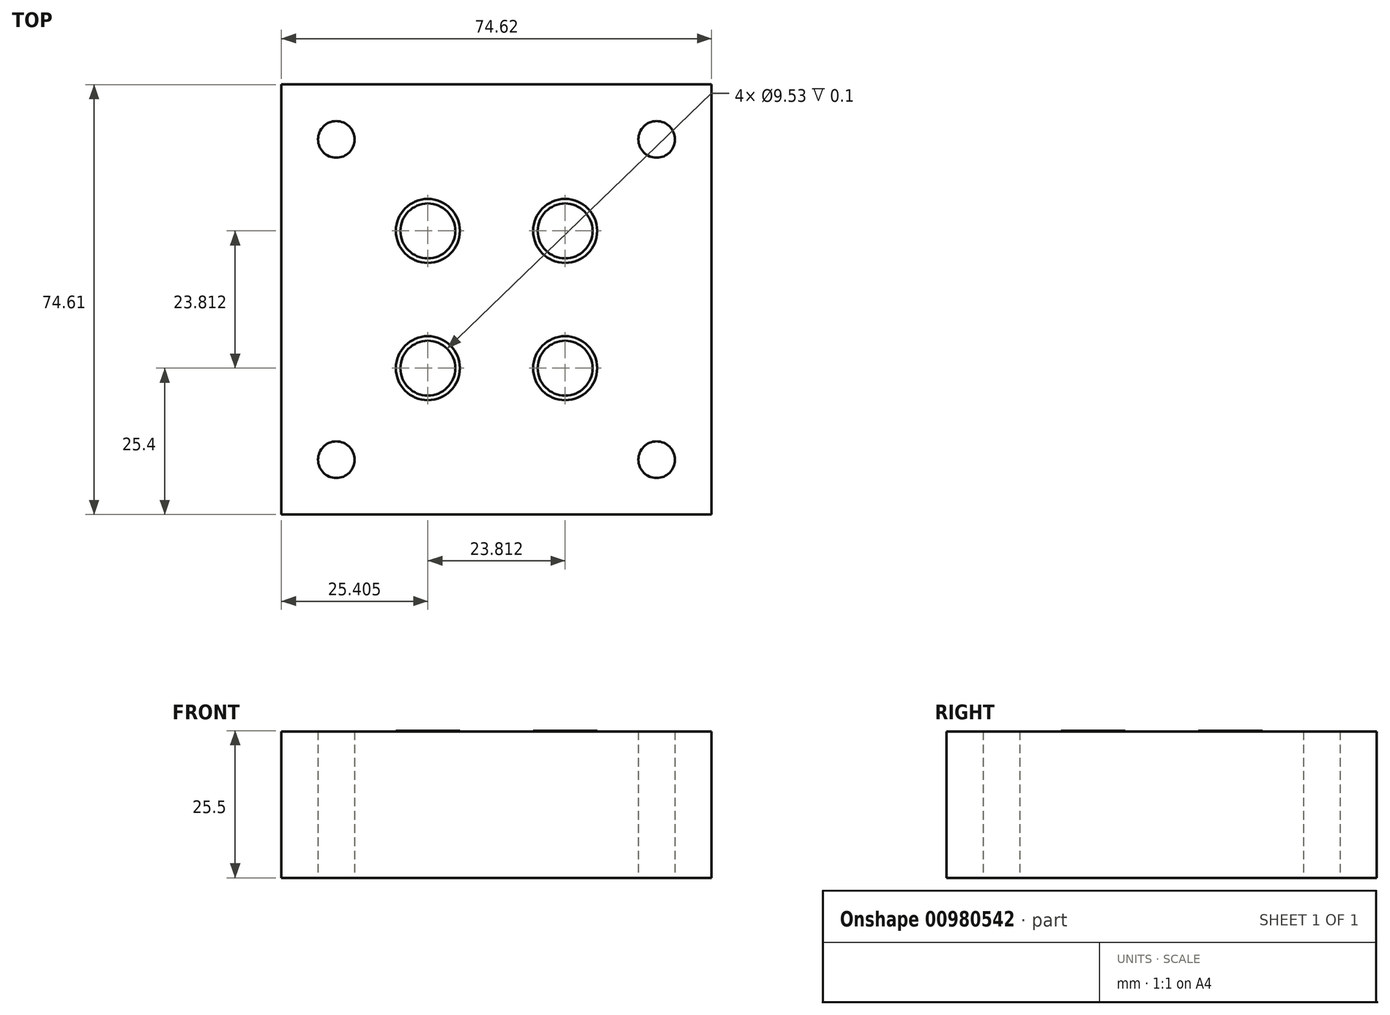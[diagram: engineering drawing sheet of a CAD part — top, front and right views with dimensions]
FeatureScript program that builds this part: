
annotation { "Feature Type Name" : "Feature", "Feature Type Description" : "" }
export const myFeature = defineFeature(function(context is Context, id is Id, definition is map)
    precondition{}
    {
        {
            var Q0;
            Q0=qCreatedBy(makeId("Top.planeOp"),FACE);
            var sketch = newSketch(context, id + "F0", { "sketchPlane" : qUnion([Q0])});
            skLineSegment(sketch, "E0.bottom", {"start": v(-258.87, 74.61) * mm, "end": v(-184.25, 74.61) * mm});
            skLineSegment(sketch, "E0.top", {"start": v(-258.87, 0) * mm, "end": v(-184.25, 0) * mm});
            skLineSegment(sketch, "E0.left", {"start": v(-258.87, 74.61) * mm, "end": v(-258.87, 0) * mm});
            skLineSegment(sketch, "E0.right", {"start": v(-184.25, 74.61) * mm, "end": v(-184.25, 0) * mm});
            skSolve(sketch);
        }
        {
            var Q0;
            Q0=makeQuery(id+"F0.imprint","IMPRINT",FACE,{"disambiguationData":[TD([[makeQuery(id+"F0.imprint","IMPRINT",EDGE,{"derivedFrom":sQuery(id+"F0.wireOp",EDGE,"E0.bottom")}),-1.0]])]});
            extrude(context, id + "F1", {"entities" : qUnion([Q0]), "depth" : 25.4 * mm, "offsetDistance" : 25.4 * mm});
        }
        {
            var Q0;
            Q0=qCreatedBy(makeId("Top.planeOp"),FACE);
            var sketch = newSketch(context, id + "F2", { "sketchPlane" : qUnion([Q0])});
            skCircle(sketch, "E1", {"center": v(-249.34, 65.09) * mm, "radius": 3.18 * mm});
            skCircle(sketch, "E2", {"center": v(-193.78, 65.09) * mm, "radius": 3.18 * mm});
            skCircle(sketch, "E3", {"center": v(-249.34, 9.53) * mm, "radius": 3.18 * mm});
            skCircle(sketch, "E4", {"center": v(-193.78, 9.52) * mm, "radius": 3.18 * mm});
            skSolve(sketch);
        }
        {
            var Q0;
            Q0 = qSketchRegion(id + "F2", true);
            extrude(context, id + "F3", {"entities" : qUnion([Q0]), "operationType" : NewBodyOperationType.REMOVE, "depth" : 25.4 * mm, "offsetDistance" : 25.4 * mm});
        }
        {
            var Q0;
            Q0=makeQuery(id+"F1.opExtrude","CAP_FACE",FACE,{"disambiguationData":[OSD([sQuery(id+"F0.wireOp",EDGE,"E0.bottom"),sQuery(id+"F0.wireOp",EDGE,"E0.top"),sQuery(id+"F0.wireOp",EDGE,"E0.left"),sQuery(id+"F0.wireOp",EDGE,"E0.right")])],"isStart":false});
            var sketch = newSketch(context, id + "F4", { "sketchPlane" : qUnion([Q0])});
            skCircle(sketch, "E5", {"center": v(-233.47, 49.21) * mm, "radius": 5.56 * mm});
            skCircle(sketch, "E6", {"center": v(-209.65, 49.21) * mm, "radius": 5.56 * mm});
            skCircle(sketch, "E7", {"center": v(-233.47, 25.4) * mm, "radius": 5.56 * mm});
            skCircle(sketch, "E8", {"center": v(-209.65, 25.4) * mm, "radius": 5.56 * mm});
            skSolve(sketch);
        }
        {
            var Q0;
            Q0 = qSketchRegion(id + "F4", true);
            extrude(context, id + "F5", {"entities" : qUnion([Q0]), "operationType" : NewBodyOperationType.ADD, "depth" : 0.1 * mm, "offsetDistance" : 25.4 * mm});
        }
        {
            var Q0;
            Q0=makeQuery(id+"F5.opExtrude","CAP_FACE",FACE,{"disambiguationData":[OSD([sQuery(id+"F4.wireOp",EDGE,"E7")])],"isStart":false});
            var sketch = newSketch(context, id + "F6", { "sketchPlane" : qUnion([Q0])});
            skCircle(sketch, "E9", {"center": v(-233.47, 25.4) * mm, "radius": 4.76 * mm});
            skCircle(sketch, "E10", {"center": v(-233.47, 49.21) * mm, "radius": 4.76 * mm});
            skCircle(sketch, "E11", {"center": v(-209.65, 25.4) * mm, "radius": 4.76 * mm});
            skCircle(sketch, "E12", {"center": v(-209.65, 49.21) * mm, "radius": 4.76 * mm});
            skSolve(sketch);
        }
        {
            var Q0;
            Q0 = qSketchRegion(id + "F6", true);
            extrude(context, id + "F7", {"entities" : qUnion([Q0]), "operationType" : NewBodyOperationType.REMOVE, "oppositeDirection" : true, "depth" : 0.1 * mm, "offsetDistance" : 25.4 * mm});
        }
    });
